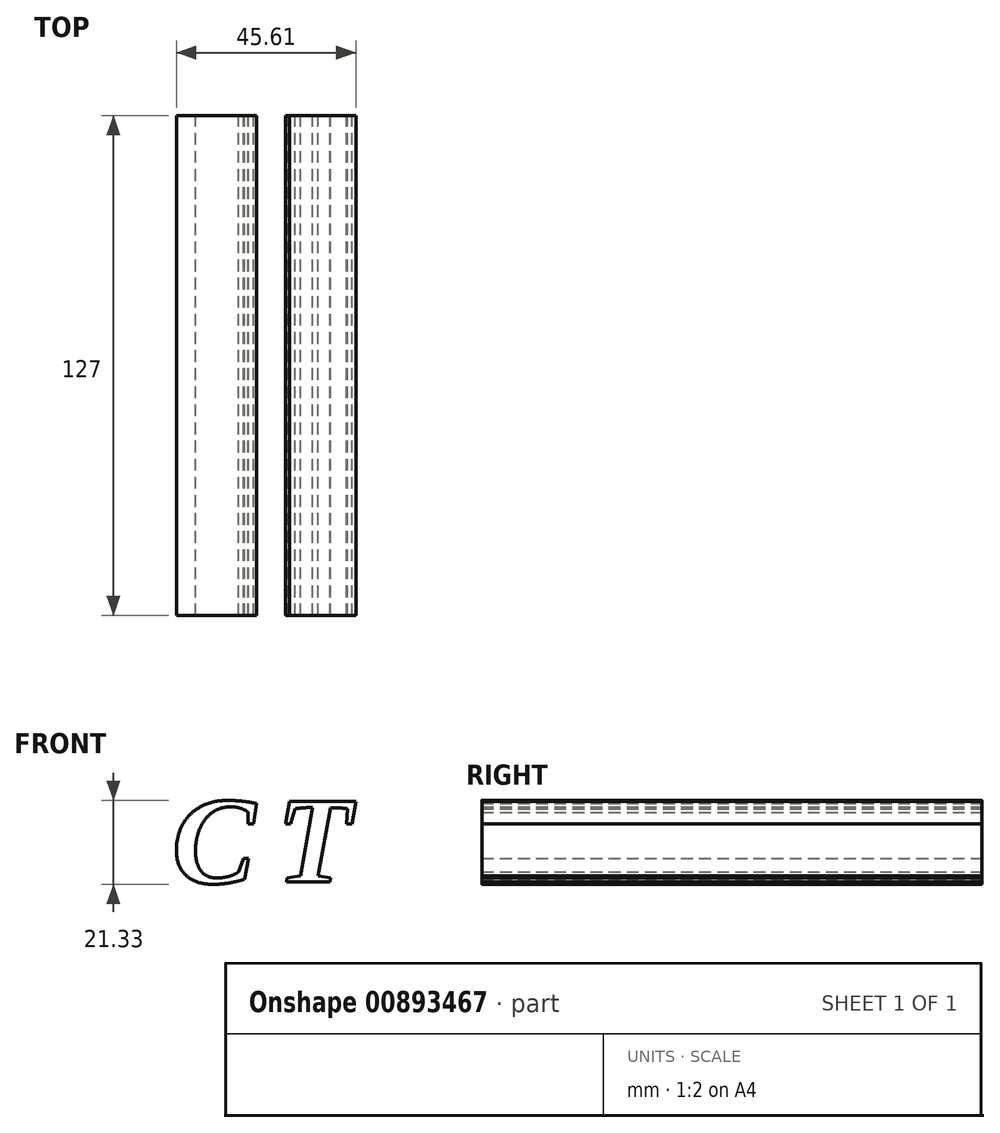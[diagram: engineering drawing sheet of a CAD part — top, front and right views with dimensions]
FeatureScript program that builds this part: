
annotation { "Feature Type Name" : "Feature", "Feature Type Description" : "" }
export const myFeature = defineFeature(function(context is Context, id is Id, definition is map)
    precondition{}
    {
        {
            var Q0;
            Q0=qCreatedBy(makeId("Front.planeOp"),FACE);
            var sketch = newSketch(context, id + "F0", { "sketchPlane" : qUnion([Q0])});
            skText(sketch, "E0", { "text": "C", "fontName": "Tinos-BoldItalic.ttf"});
            skText(sketch, "E1", { "text": "T", "fontName": "Tinos-BoldItalic.ttf"});
            const initialGuessF0  = {"E0": [-0.02023, -0.00412, 1, 0, 0.02286], "E1": [0.00627, -0.00386, 1, 0, 0.0226]};
            skSetInitialGuess(sketch, initialGuessF0);
            skSolve(sketch);
        }
        {
            var Q0;
            Q0 = qSketchRegion(id + "F0", true);
            var Q1;
            Q1 = qConstructionFilter(qBodyType(qCreatedBy(id + "F0" ,EDGE), BodyType.WIRE), ConstructionObject.NO);
            extrude(context, id + "F1", {"entities" : qUnion([Q0]), "surfaceEntities" : qUnion([Q1]), "depth" : 127 * mm, "offsetDistance" : 25.4 * mm});
        }
    });
